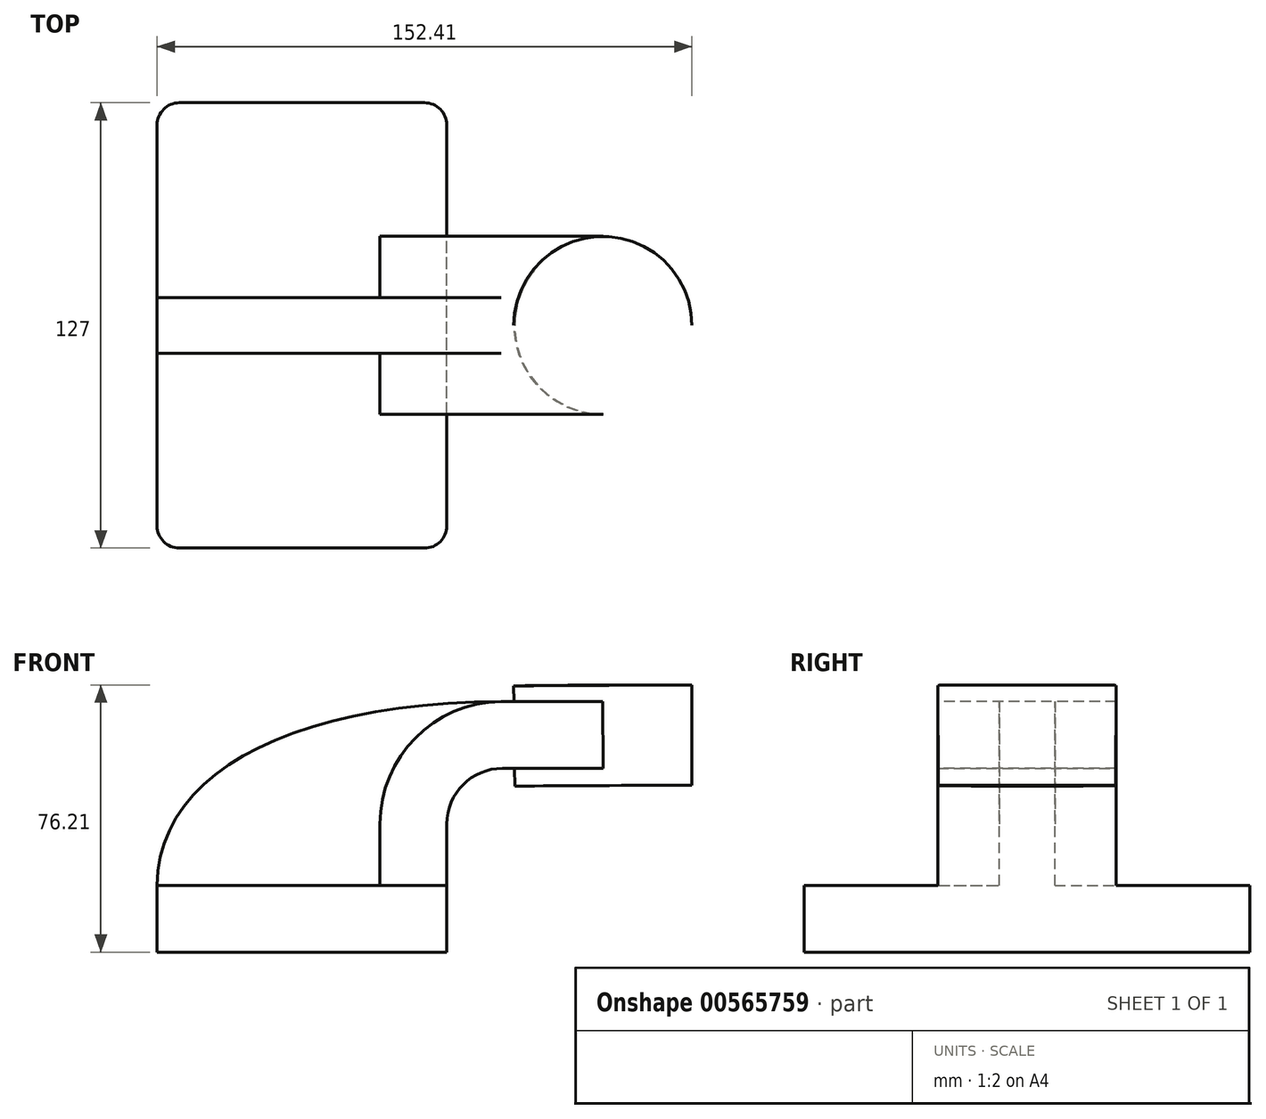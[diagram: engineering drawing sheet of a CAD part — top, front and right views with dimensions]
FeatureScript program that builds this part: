
annotation { "Feature Type Name" : "Feature", "Feature Type Description" : "" }
export const myFeature = defineFeature(function(context is Context, id is Id, definition is map)
    precondition{}
    {
        {
            var Q0;
            Q0=qCreatedBy(makeId("Front.planeOp"),FACE);
            var sketch = newSketch(context, id + "F0", { "sketchPlane" : qUnion([Q0])});
            skLineSegment(sketch, "E0.bottom", {"start": v(-41.27, -9.52) * mm, "end": v(41.28, -9.52) * mm});
            skLineSegment(sketch, "E0.top", {"start": v(-41.28, 9.53) * mm, "end": v(41.28, 9.53) * mm});
            skLineSegment(sketch, "E0.left", {"start": v(-41.28, -9.52) * mm, "end": v(-41.28, 9.53) * mm});
            skLineSegment(sketch, "E0.right", {"start": v(41.28, -9.52) * mm, "end": v(41.28, 9.53) * mm});
            skPoint(sketch, "E0.middle", {"position": v(0, 0) * mm});
            skLineSegment(sketch, "E1.bottom", {"start": v(111.13, 38.1) * mm, "end": v(60.33, 38.1) * mm});
            skLineSegment(sketch, "E1.top", {"start": v(111.13, 66.67) * mm, "end": v(60.33, 66.67) * mm});
            skLineSegment(sketch, "E1.left", {"start": v(111.13, 38.1) * mm, "end": v(111.13, 66.68) * mm});
            skLineSegment(sketch, "E1.right", {"start": v(60.33, 38.1) * mm, "end": v(60.33, 66.68) * mm});
            skPoint(sketch, "E1.middle", {"position": v(85.73, 52.39) * mm});
            skLineSegment(sketch, "E2", {"start": v(41.27, 9.53) * mm, "end": v(41.27, 27) * mm});
            skArc(sketch, "E3", {"start": v(41.27, 27) * mm, "mid": v(45.92, 38.23) * mm, "end": v(57.15, 42.88) * mm});
            skLineSegment(sketch, "E4", {"start": v(57.15, 42.88) * mm, "end": v(85.88, 42.88) * mm});
            skLineSegment(sketch, "E5.0", {"start": v(57.15, 61.93) * mm, "end": v(85.75, 61.93) * mm});
            skArc(sketch, "E5.1", {"start": v(22.22, 27) * mm, "mid": v(32.45, 51.7) * mm, "end": v(57.15, 61.93) * mm});
            skLineSegment(sketch, "E5.2", {"start": v(22.22, 9.53) * mm, "end": v(22.22, 27) * mm});
            skLineSegment(sketch, "E6", {"start": v(85.73, 66.68) * mm, "end": v(85.88, 38.1) * mm});
            skFitSpline(sketch, "E7", {"points": [v(-41.28, 9.53) * mm, v(57.15, 61.93) * mm], "startDerivative": vector(0.87, 96.23) * mm, "endDerivative": vector(180.7, 0.89) * mm});
            skSolve(sketch);
        }
        {
            var Q0;
            Q0=makeQuery(id+"F0.imprint","IMPRINT",FACE,{"disambiguationData":[TD([[makeQuery(id+"F0.imprint","IMPRINT",EDGE,{"derivedFrom":sQuery(id+"F0.wireOp",EDGE,"E0.bottom")}),1.0]])]});
            extrude(context, id + "F1", {"entities" : qUnion([Q0]), "endBound" : BoundingType.SYMMETRIC, "depth" : 127 * mm, "offsetDistance" : 25.4 * mm});
        }
        {
            var Q0;
            {var subQ1=sQuery(id+"F0.wireOp",EDGE,"E2");Q0=makeQuery(id+"F0.imprint","IMPRINT",FACE,{"disambiguationData":[TD([[makeQuery(id+"F0.imprint","IMPRINT",EDGE,{"derivedFrom":subQ1}),1.0]])]});}
            var Q1;
            {var subQ0=sQuery(id+"F0.wireOp",EDGE,"E4");var subQ1=sQuery(id+"F0.wireOp",EDGE,"E1.right");var subQ2=makeQuery(id+"F0.imprint","INTERSECT",VERTEX,{"derivedFrom":[subQ1,subQ0]});Q1=makeQuery(id+"F0.imprint","IMPRINT",FACE,{"disambiguationData":[TD([[makeQuery(id+"F0.imprint","IMPRINT",EDGE,{"disambiguationData":[TD([[subQ2,-1.0]])],"derivedFrom":subQ1}),-1.0]])]});}
            extrude(context, id + "F2", {"entities" : qUnion([Q0, Q1]), "operationType" : NewBodyOperationType.ADD, "endBound" : BoundingType.SYMMETRIC, "depth" : 50.8 * mm, "offsetDistance" : 25.4 * mm});
        }
        {
            var Q0;
            {var subQ3=sQuery(id+"F0.wireOp",EDGE,"E5.2");Q0=makeQuery(id+"F0.imprint","IMPRINT",FACE,{"disambiguationData":[TD([[makeQuery(id+"F0.imprint","IMPRINT",EDGE,{"derivedFrom":subQ3}),1.0]])]});}
            extrude(context, id + "F3", {"entities" : qUnion([Q0]), "operationType" : NewBodyOperationType.ADD, "endBound" : BoundingType.SYMMETRIC, "depth" : 15.88 * mm, "offsetDistance" : 25.4 * mm});
        }
        {
            var Q0;
            {var subQ0=sQuery(id+"F0.wireOp",EDGE,"E1.left");Q0=makeQuery(id+"F0.imprint","IMPRINT",FACE,{"disambiguationData":[TD([[makeQuery(id+"F0.imprint","IMPRINT",EDGE,{"derivedFrom":subQ0}),1.0]])]});}
            var Q1;
            Q1=sQuery(id+"F0.wireOp",EDGE,"E6");
            revolve(context, id + "F4", {"operationType" : NewBodyOperationType.ADD, "entities" : qUnion([Q0]), "axis" : qUnion([Q1]), "revolveType" : RevolveType.FULL});
        }
        {
            var Q0;
            Q0=makeQuery(id+"F1.opExtrude","CAP_EDGE",EDGE,{"disambiguationData":[OSD([sQuery(id+"F0.wireOp",EDGE,"E0.right")])],"isStart":false});
            var Q1;
            Q1=makeQuery(id+"F1.opExtrude","CAP_EDGE",EDGE,{"disambiguationData":[OSD([sQuery(id+"F0.wireOp",EDGE,"E0.left")])],"isStart":false});
            var Q2;
            Q2=makeQuery(id+"F1.opExtrude","CAP_EDGE",EDGE,{"disambiguationData":[OSD([sQuery(id+"F0.wireOp",EDGE,"E0.right")])],"isStart":true});
            var Q3;
            Q3=makeQuery(id+"F1.opExtrude","CAP_EDGE",EDGE,{"disambiguationData":[OSD([sQuery(id+"F0.wireOp",EDGE,"E0.left")])],"isStart":true});
            fillet(context, id + "F5", {"entities" : qUnion([Q0, Q1, Q2, Q3]), "radius" : 6.35 * mm, "tangentPropagation" : true, "allowEdgeOverflow" : false});
        }
    });
